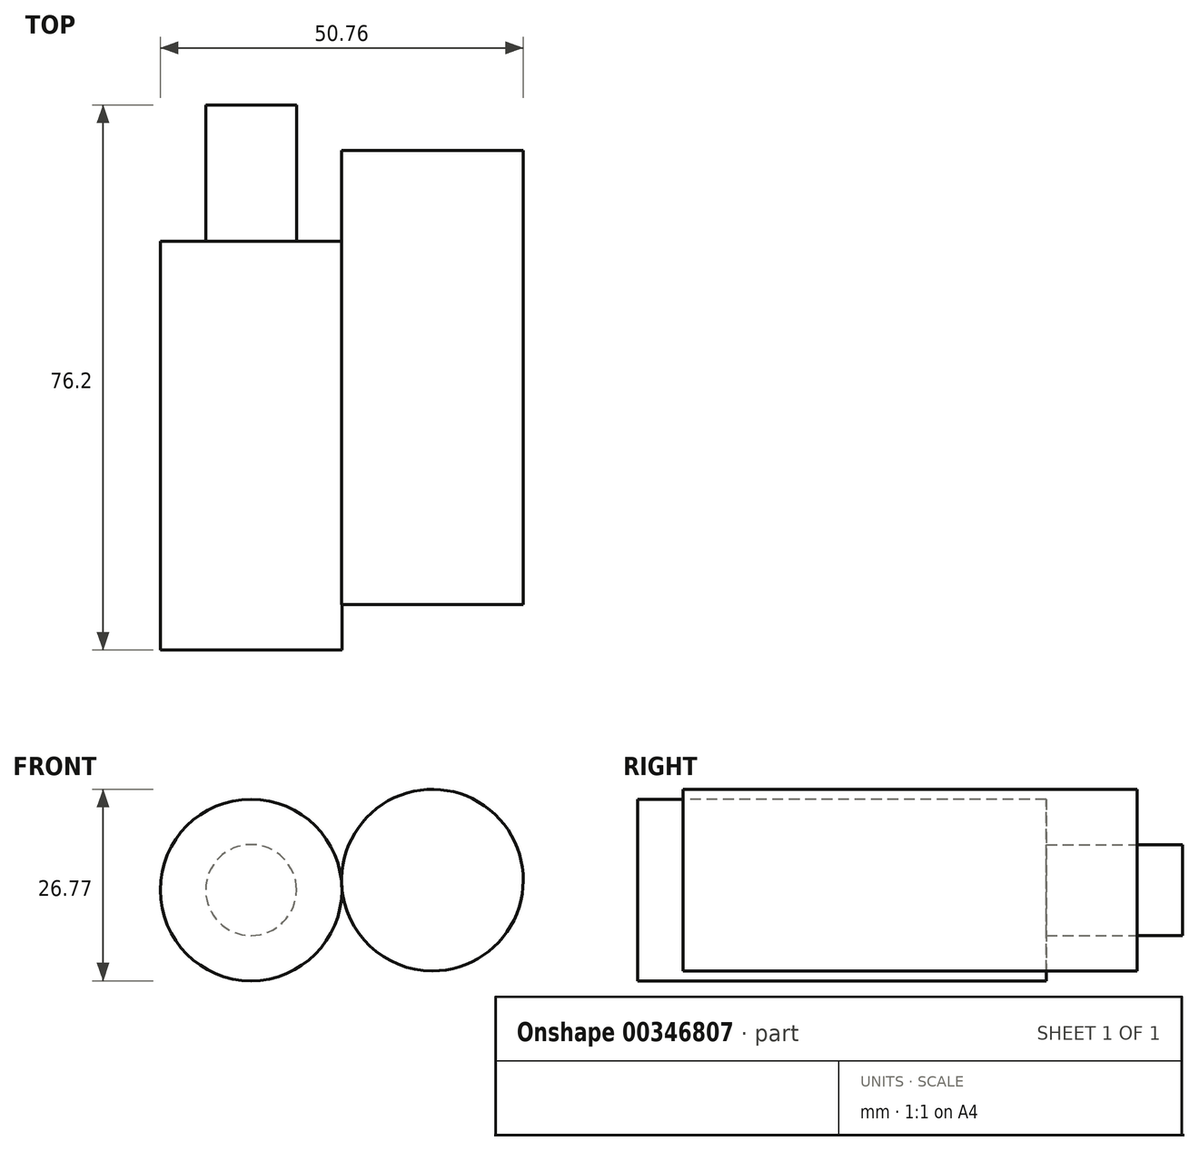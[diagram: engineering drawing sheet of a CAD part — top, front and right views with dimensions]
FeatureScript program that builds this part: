
annotation { "Feature Type Name" : "Feature", "Feature Type Description" : "" }
export const myFeature = defineFeature(function(context is Context, id is Id, definition is map)
    precondition{}
    {
        {
            var Q0;
            Q0=qCreatedBy(makeId("Front.planeOp"),FACE);
            var sketch = newSketch(context, id + "F0", { "sketchPlane" : qUnion([Q0])});
            skCircle(sketch, "E0", {"center": v(-42.8, 36.56) * mm, "radius": 6.35 * mm});
            skCircle(sketch, "E1", {"center": v(-42.8, 36.56) * mm, "radius": 19.05 * mm});
            skSolve(sketch);
        }
        {
            var Q0;
            Q0=makeQuery(id+"F0.imprint","IMPRINT",FACE,{"disambiguationData":[TD([[makeQuery(id+"F0.imprint","IMPRINT",EDGE,{"derivedFrom":sQuery(id+"F0.wireOp",EDGE,"E0")}),1.0]])]});
            extrude(context, id + "F1", {"entities" : qUnion([Q0]), "endBound" : BoundingType.SYMMETRIC, "depth" : 76.2 * mm});
        }
        {
            var Q0;
            Q0=makeQuery(id+"F1.opExtrude","CAP_FACE",FACE,{"disambiguationData":[OSD([sQuery(id+"F0.wireOp",EDGE,"E0")])],"isStart":false});
            var sketch = newSketch(context, id + "F2", { "sketchPlane" : qUnion([Q0])});
            skCircle(sketch, "E2", {"center": v(-42.8, 36.56) * mm, "radius": 12.7 * mm});
            skSolve(sketch);
        }
        {
            var Q0;
            Q0=makeQuery(id+"F2.imprint","IMPRINT",FACE,{"disambiguationData":[TD([[makeQuery(id+"F2.imprint","IMPRINT",EDGE,{"derivedFrom":sQuery(id+"F2.wireOp",EDGE,"E2")}),1.0]])]});
            extrude(context, id + "F3", {"entities" : qUnion([Q0]), "operationType" : NewBodyOperationType.ADD, "oppositeDirection" : true, "depth" : 57.15 * mm});
        }
        {
            var Q0;
            Q0=qCreatedBy(makeId("Front.planeOp"),FACE);
            var sketch = newSketch(context, id + "F4", { "sketchPlane" : qUnion([Q0])});
            skCircle(sketch, "E3", {"center": v(-17.44, 37.93) * mm, "radius": 12.7 * mm});
            skCircle(sketch, "E4", {"center": v(-17.44, 37.93) * mm, "radius": 6.35 * mm});
            skSolve(sketch);
        }
        {
            var Q0;
            Q0 = qSketchRegion(id + "F4", true);
            var Q1;
            Q1=makeQuery(id+"F4.imprint","IMPRINT",FACE,{"disambiguationData":[TD([[makeQuery(id+"F4.imprint","IMPRINT",EDGE,{"derivedFrom":sQuery(id+"F4.wireOp",EDGE,"E4")}),1.0]])]});
            extrude(context, id + "F5", {"entities" : qUnion([Q0, Q1]), "endBound" : BoundingType.SYMMETRIC, "oppositeDirection" : true, "depth" : 63.5 * mm});
        }
    });
